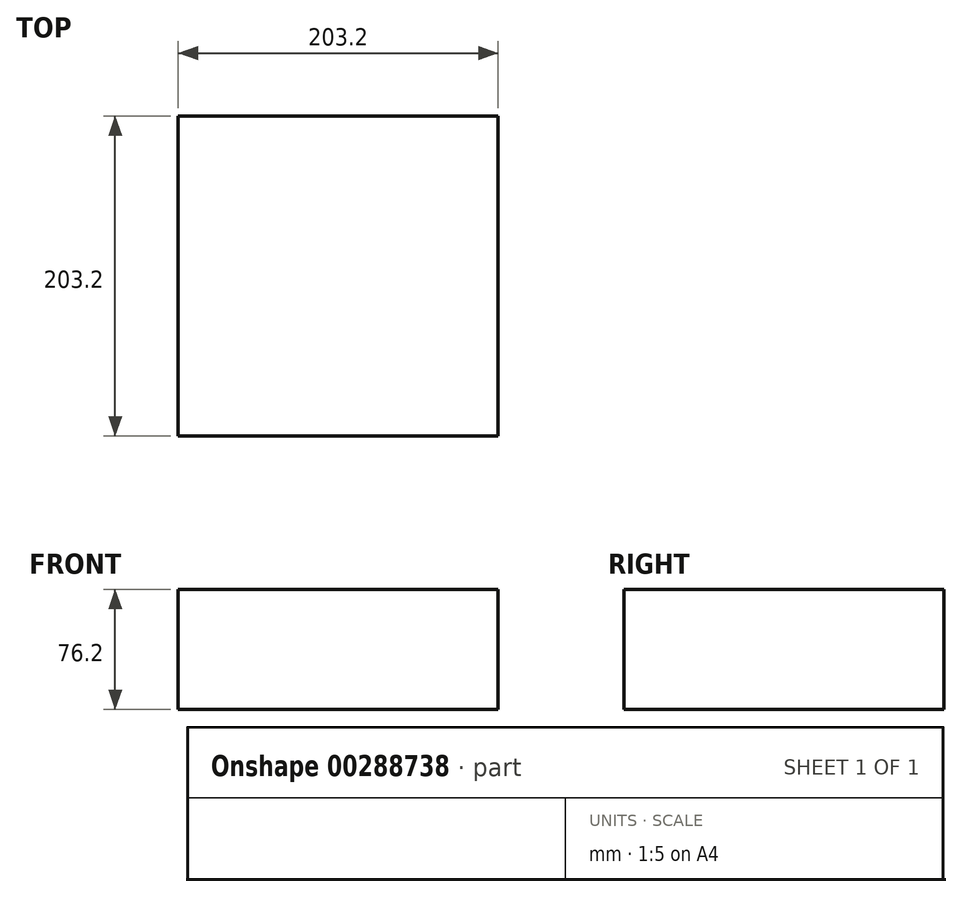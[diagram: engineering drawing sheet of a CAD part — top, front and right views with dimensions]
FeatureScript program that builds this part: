
annotation { "Feature Type Name" : "Feature", "Feature Type Description" : "" }
export const myFeature = defineFeature(function(context is Context, id is Id, definition is map)
    precondition{}
    {
        {
            var Q0;
            Q0=qCreatedBy(makeId("Top.planeOp"),FACE);
            var sketch = newSketch(context, id + "F0", { "sketchPlane" : qUnion([Q0])});
            skLineSegment(sketch, "E0.bottom", {"start": v(101.6, 101.6) * mm, "end": v(-101.6, 101.6) * mm});
            skLineSegment(sketch, "E0.top", {"start": v(101.6, -101.6) * mm, "end": v(-101.6, -101.6) * mm});
            skLineSegment(sketch, "E0.left", {"start": v(101.6, 101.6) * mm, "end": v(101.6, -101.6) * mm});
            skLineSegment(sketch, "E0.right", {"start": v(-101.6, 101.6) * mm, "end": v(-101.6, -101.6) * mm});
            skPoint(sketch, "E0.middle", {"position": v(0, 0) * mm});
            skSolve(sketch);
        }
        {
            var Q0;
            Q0=qSketchRegion(id+"F0",true);
            extrude(context, id + "F1", {"entities" : qUnion([Q0]), "endBound" : BoundingType.SYMMETRIC, "depth" : 76.2 * mm});
        }
    });
